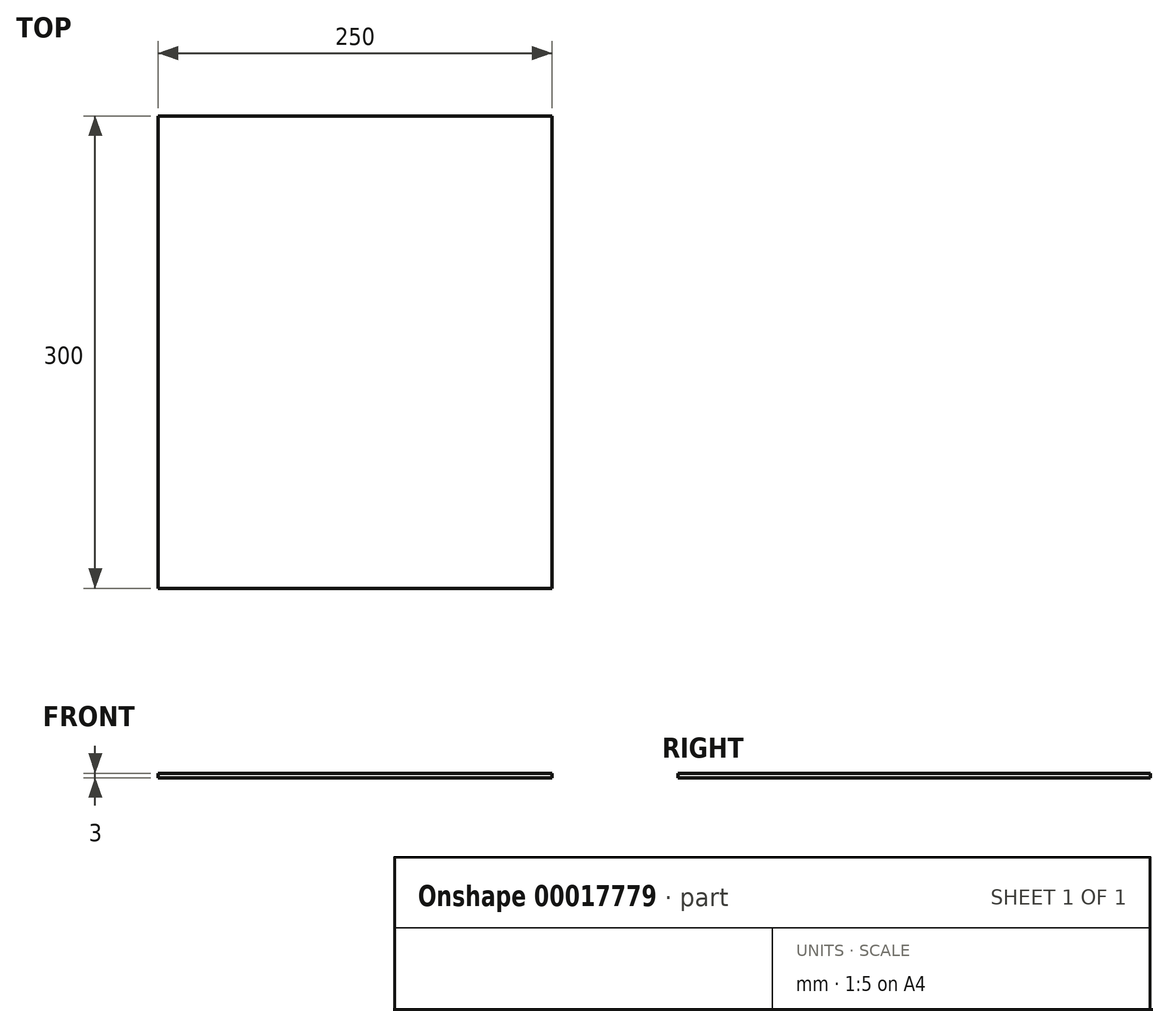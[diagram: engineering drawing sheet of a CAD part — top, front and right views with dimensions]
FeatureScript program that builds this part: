
annotation { "Feature Type Name" : "Feature", "Feature Type Description" : "" }
export const myFeature = defineFeature(function(context is Context, id is Id, definition is map)
    precondition{}
    {
        {
            var Q0;
            Q0=qCreatedBy(makeId("Top.planeOp"),FACE);
            var sketch = newSketch(context, id + "F0", { "sketchPlane" : qUnion([Q0])});
            skLineSegment(sketch, "E0.bottom", {"start": v(0, 0) * mm, "end": v(250, 0) * mm});
            skLineSegment(sketch, "E0.top", {"start": v(0, 300) * mm, "end": v(250, 300) * mm});
            skLineSegment(sketch, "E0.left", {"start": v(0, 0) * mm, "end": v(0, 300) * mm});
            skLineSegment(sketch, "E0.right", {"start": v(250, 0) * mm, "end": v(250, 300) * mm});
            skSolve(sketch);
        }
        {
            var Q0;
            Q0=qSketchRegion(id+"F0",true);
            extrude(context, id + "F1", {"entities" : qUnion([Q0]), "depth" : 3 * mm});
        }
    });
